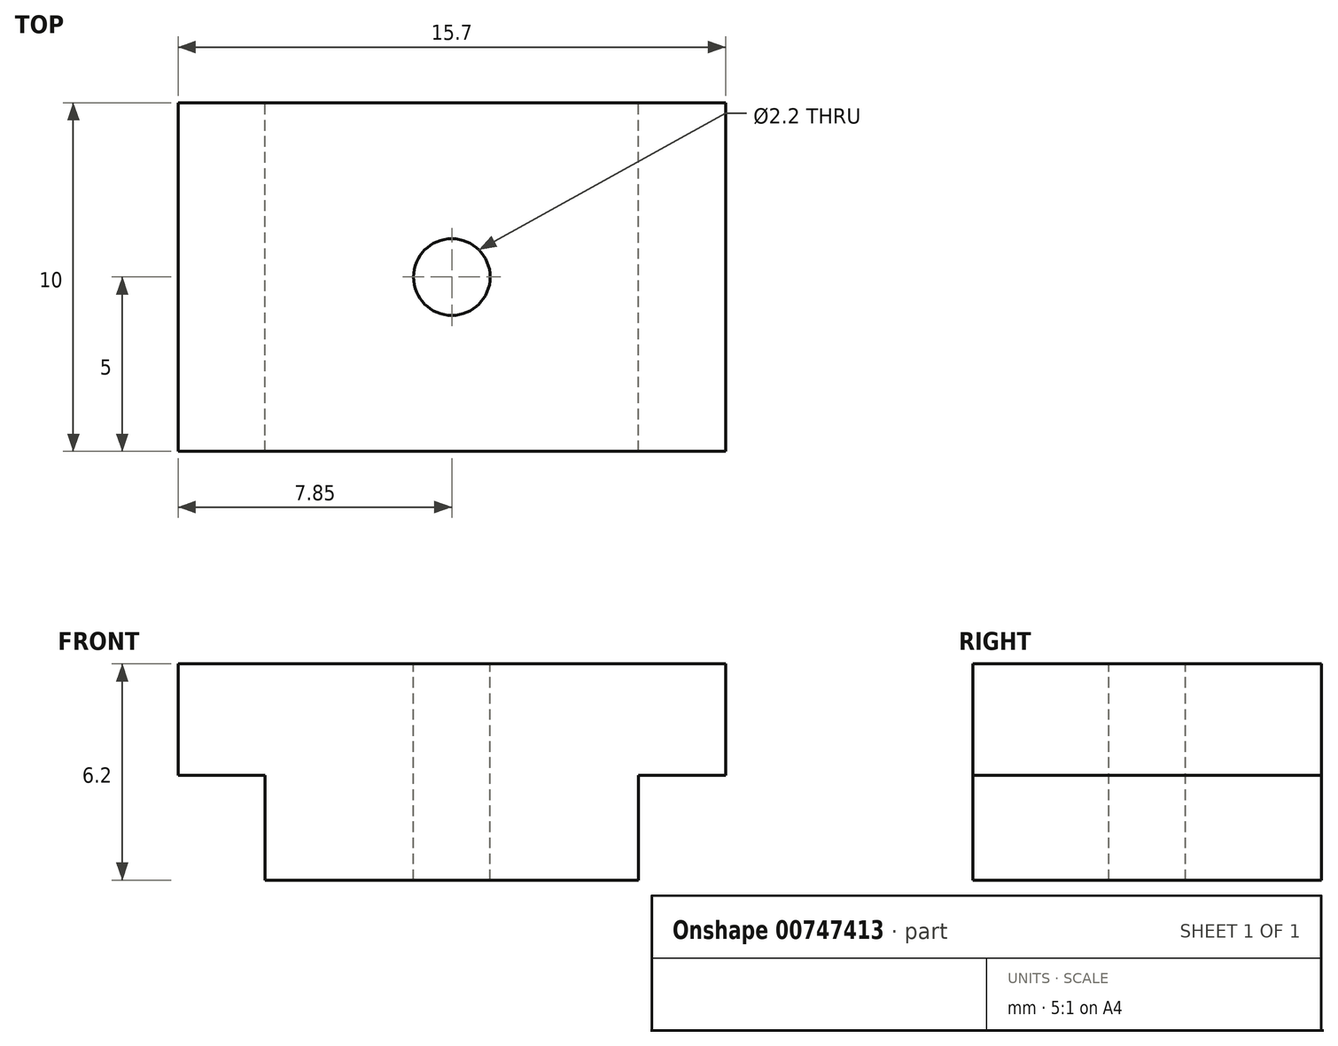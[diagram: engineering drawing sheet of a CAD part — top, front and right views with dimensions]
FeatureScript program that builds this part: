
annotation { "Feature Type Name" : "Feature", "Feature Type Description" : "" }
export const myFeature = defineFeature(function(context is Context, id is Id, definition is map)
    precondition{}
    {
        {
            var Q0;
            Q0=qCreatedBy(makeId("Front.planeOp"),FACE);
            var sketch = newSketch(context, id + "F0", { "sketchPlane" : qUnion([Q0])});
            skLineSegment(sketch, "E0", {"start": v(-5.35, 0) * mm, "end": v(5.35, 0) * mm});
            skLineSegment(sketch, "E1", {"start": v(5.35, 0) * mm, "end": v(5.35, 3) * mm});
            skLineSegment(sketch, "E2", {"start": v(5.35, 3) * mm, "end": v(7.85, 3) * mm});
            skLineSegment(sketch, "E3", {"start": v(7.85, 3) * mm, "end": v(7.85, 6.2) * mm});
            skLineSegment(sketch, "E4", {"start": v(7.85, 6.2) * mm, "end": v(-7.85, 6.2) * mm});
            skLineSegment(sketch, "E5", {"start": v(-7.85, 6.2) * mm, "end": v(-7.85, 3) * mm});
            skLineSegment(sketch, "E6", {"start": v(-7.85, 3) * mm, "end": v(-5.35, 3) * mm});
            skLineSegment(sketch, "E7", {"start": v(-5.35, 3) * mm, "end": v(-5.35, 0) * mm});
            skSolve(sketch);
        }
        {
            var Q0;
            Q0 = qSketchRegion(id + "F0", true);
            extrude(context, id + "F1", {"entities" : qUnion([Q0]), "depth" : 10 * mm, "offsetDistance" : 25 * mm});
        }
        {
            var Q0;
            Q0=makeQuery(id+"F1.opExtrude","SWEPT_FACE",FACE,{"disambiguationData":[OSD([sQuery(id+"F0.wireOp",EDGE,"E4")])]});
            var sketch = newSketch(context, id + "F2", { "sketchPlane" : qUnion([Q0])});
            skCircle(sketch, "E8", {"center": v(0, -5) * mm, "radius": 1.1 * mm});
            skLineSegment(sketch, "E9", {"start": v(-7.85, 0) * mm, "end": v(7.85, -10) * mm, "construction": true});
            skSolve(sketch);
        }
        {
            var Q0;
            Q0 = qSketchRegion(id + "F2", true);
            extrude(context, id + "F3", {"entities" : qUnion([Q0]), "operationType" : NewBodyOperationType.REMOVE, "endBound" : BoundingType.UP_TO_NEXT, "oppositeDirection" : true, "depth" : 25 * mm, "offsetDistance" : 25 * mm});
        }
    });
